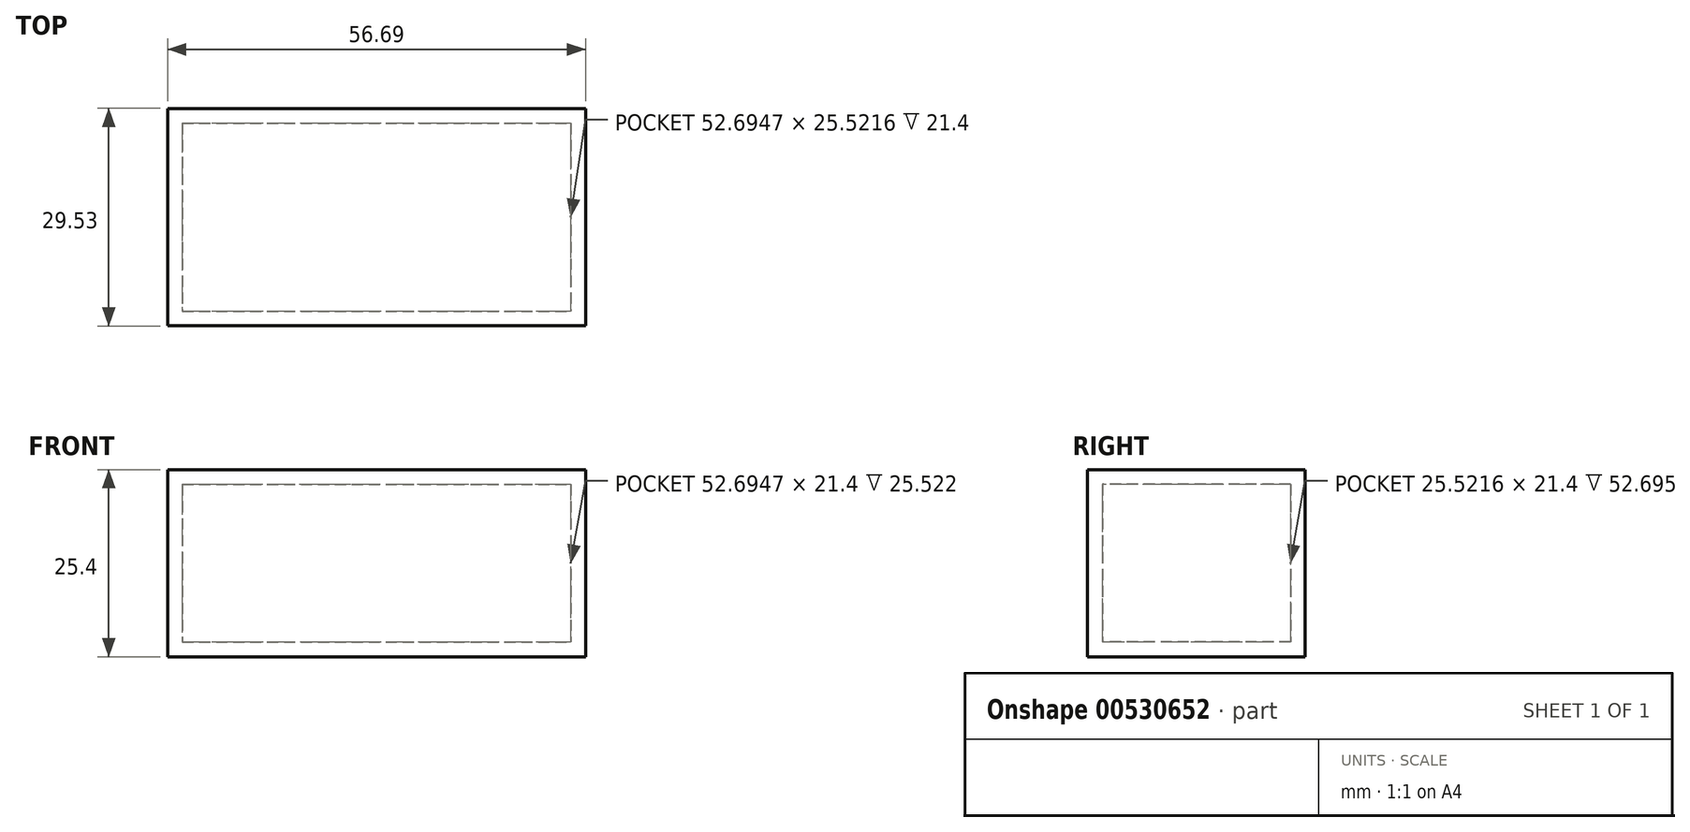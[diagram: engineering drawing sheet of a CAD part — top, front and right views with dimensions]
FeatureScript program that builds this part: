
annotation { "Feature Type Name" : "Feature", "Feature Type Description" : "" }
export const myFeature = defineFeature(function(context is Context, id is Id, definition is map)
    precondition{}
    {
        {
            var Q0;
            Q0=qCreatedBy(makeId("Top.planeOp"),FACE);
            var sketch = newSketch(context, id + "F0", { "sketchPlane" : qUnion([Q0])});
            skLineSegment(sketch, "E0.bottom", {"start": v(-25, 12.92) * mm, "end": v(31.7, 12.92) * mm});
            skLineSegment(sketch, "E0.top", {"start": v(-25, -16.6) * mm, "end": v(31.7, -16.6) * mm});
            skLineSegment(sketch, "E0.left", {"start": v(-25, 12.92) * mm, "end": v(-25, -16.6) * mm});
            skLineSegment(sketch, "E0.right", {"start": v(31.7, 12.92) * mm, "end": v(31.7, -16.6) * mm});
            skSolve(sketch);
        }
        {
            var Q0;
            Q0=makeQuery(id+"F0.imprint","IMPRINT",FACE,{"disambiguationData":[TD([[makeQuery(id+"F0.imprint","IMPRINT",EDGE,{"derivedFrom":sQuery(id+"F0.wireOp",EDGE,"E0.bottom")}),-1.0]])]});
            extrude(context, id + "F1", {"entities" : qUnion([Q0]), "depth" : 25.4 * mm, "offsetDistance" : 25.4 * mm});
        }
        {
            var Q0;
            Q0=makeQuery(id+"F1.opExtrude","CAP_FACE",FACE,{"disambiguationData":[OSD([sQuery(id+"F0.wireOp",EDGE,"E0.bottom"),sQuery(id+"F0.wireOp",EDGE,"E0.top"),sQuery(id+"F0.wireOp",EDGE,"E0.left"),sQuery(id+"F0.wireOp",EDGE,"E0.right")])],"isStart":false});
            var Q1;
            Q1=makeQuery(id+"F1.opExtrude","SWEPT_BODY",BODY,{"disambiguationData":[OSD([sQuery(id+"F0.wireOp",EDGE,"E0.bottom"),sQuery(id+"F0.wireOp",EDGE,"E0.top"),sQuery(id+"F0.wireOp",EDGE,"E0.left"),sQuery(id+"F0.wireOp",EDGE,"E0.right")])]});
            shell(context, id + "F2", {"isHollow" : true, "entities" : qUnion([Q0]), "parts" : qUnion([Q1]), "thickness" : 2 * mm});
        }
    });
